# Revit family: Upper_Cabinets-Teknion-CEUMS_Upper_Cabinet_Microwave_Section_And_Door-R2022
name_source: partatom
category: Furniture
units: mm (PartAtom-declared; Revit-internal decimal feet)

## family parameters
Always vertical = Yes
Cut with Voids When Loaded = No
Enable Cutting in Views = No
OmniClass Number = 23.40.20.00
OmniClass Title = General Furniture and Specialties
Render Appearance Source = Family Geometry
Room Calculation Point = No
Shared = Yes
Work Plane-Based = No

## types (1)
- 15" Depth
    Assembly Code = E2020200
    Available Depth = 15 Inch Only
    Default Elevation = 0 "
    Depth = 15 "
    Description = Upper Cabinet - Microwave Section And Doors, 15" Depth
    Handle = Yes
    Manufacturer = Teknion
    Manufacturer Fax = 416.661.4586
    Model = CEUMS15____
    Part Number = CEUMS
    Product Documentation Link = https://www.teknion.com
    Product Line = Upper Cabinets
    Product Page URL = https://www.teknion.com
    Series = Expansion Casework+
    Sustainability Data = https://www.teknion.com
    URL = www.teknion.com
    Unit Weight URL = http://www.teknion.com
    Warranty = http://www.teknion.com

## geometry (parser evidence)
native form markers: Sweep x3
no freeform markers — native parametric forms only
